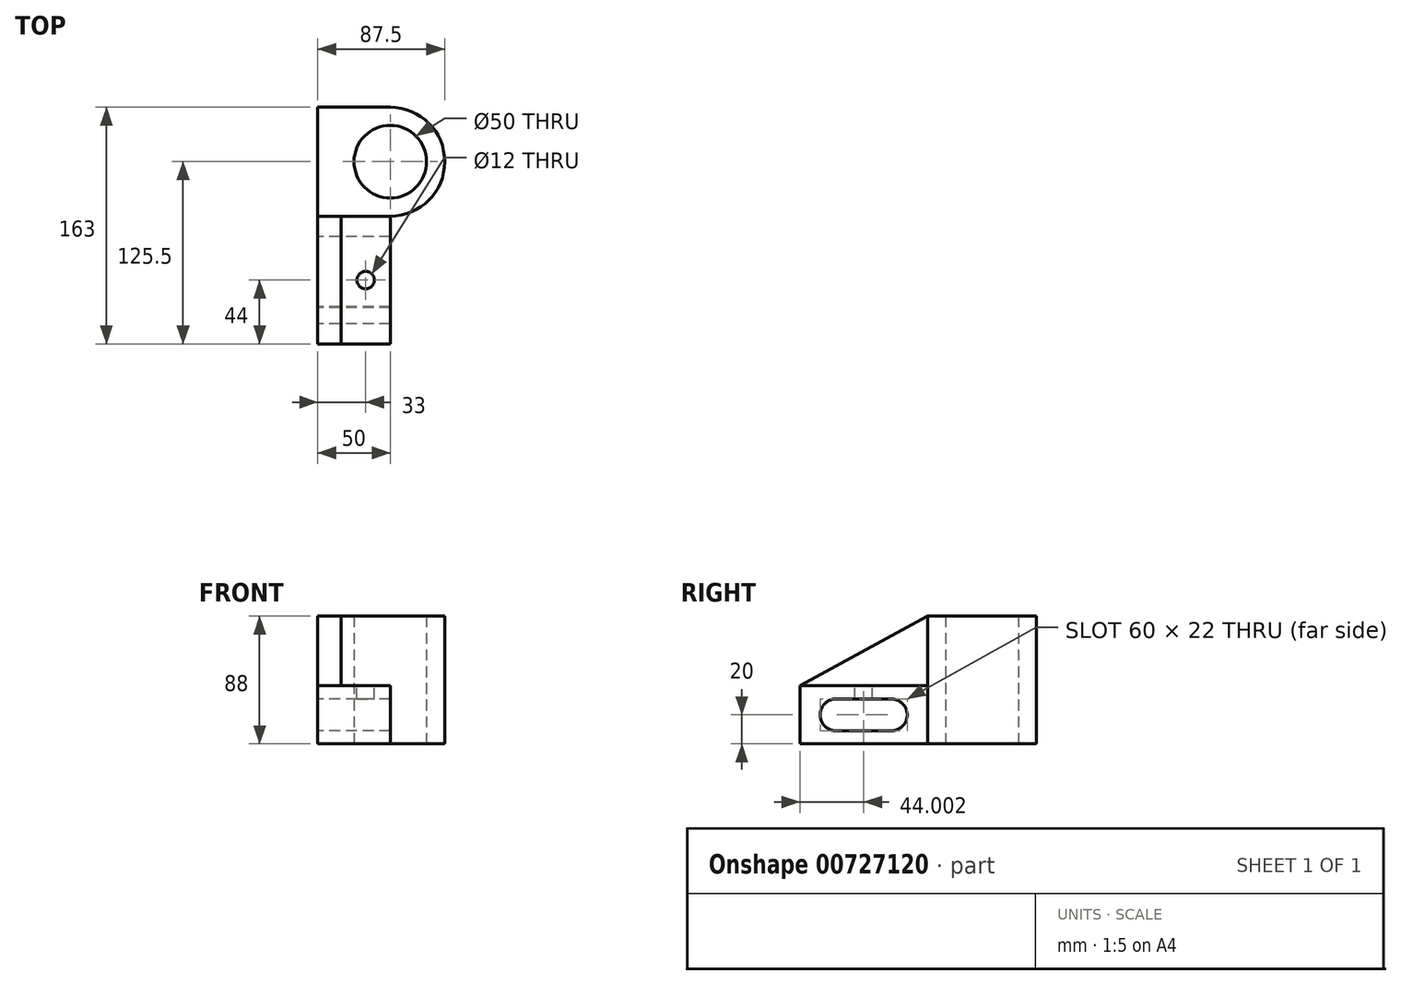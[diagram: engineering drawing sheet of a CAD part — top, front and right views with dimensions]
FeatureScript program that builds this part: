
annotation { "Feature Type Name" : "Feature", "Feature Type Description" : "" }
export const myFeature = defineFeature(function(context is Context, id is Id, definition is map)
    precondition{}
    {
        {
            var Q0;
            Q0=qCreatedBy(makeId("Top.planeOp"),FACE);
            var sketch = newSketch(context, id + "F0", { "sketchPlane" : qUnion([Q0])});
            skLineSegment(sketch, "E0.bottom", {"start": v(0, 0) * mm, "end": v(50, 0) * mm});
            skLineSegment(sketch, "E0.top", {"start": v(0, 75) * mm, "end": v(50, 75) * mm});
            skLineSegment(sketch, "E0.left", {"start": v(0, 0) * mm, "end": v(0, 75) * mm});
            skCircle(sketch, "E1", {"center": v(50, 37.5) * mm, "radius": 25 * mm});
            skCircle(sketch, "E2", {"center": v(50, 37.5) * mm, "radius": 37.5 * mm});
            skSolve(sketch);
        }
        {
            var Q0;
            Q0 = qSketchRegion(id + "F0", true);
            extrude(context, id + "F1", {"entities" : qUnion([Q0]), "depth" : 88 * mm, "offsetDistance" : 25 * mm});
        }
        {
            var Q0;
            Q0=qCreatedBy(makeId("Right.planeOp"),FACE);
            var sketch = newSketch(context, id + "F2", { "sketchPlane" : qUnion([Q0])});
            skLineSegment(sketch, "E3.bottom", {"start": v(0, 0) * mm, "end": v(-88, 0) * mm});
            skLineSegment(sketch, "E3.top", {"start": v(0, 40) * mm, "end": v(-88, 40) * mm});
            skLineSegment(sketch, "E3.left", {"start": v(0, 0) * mm, "end": v(0, 40) * mm});
            skLineSegment(sketch, "E3.right", {"start": v(-88, 0) * mm, "end": v(-88, 40) * mm});
            skLineSegment(sketch, "E4", {"start": v(0, 0) * mm, "end": v(0, 20) * mm});
            skLineSegment(sketch, "E5", {"start": v(0, 20) * mm, "end": v(-25, 20) * mm});
            skArc(sketch, "E6", {"start": v(-25, 9) * mm, "mid": v(-14, 20) * mm, "end": v(-25, 31) * mm});
            skArc(sketch, "E7", {"start": v(-62.86, 31) * mm, "mid": v(-74, 19.72) * mm, "end": v(-62.3, 9.02) * mm});
            skLineSegment(sketch, "E8", {"start": v(-63.72, 9.02) * mm, "end": v(-25, 9) * mm});
            skLineSegment(sketch, "E9", {"start": v(-63.14, 31) * mm, "end": v(-25, 31) * mm});
            skSolve(sketch);
        }
        {
            var Q0;
            Q0 = qSketchRegion(id + "F2", true);
            extrude(context, id + "F3", {"entities" : qUnion([Q0]), "operationType" : NewBodyOperationType.ADD, "depth" : 50 * mm, "offsetDistance" : 25 * mm});
        }
        {
            var Q0;
            Q0=qCreatedBy(makeId("Right.planeOp"),FACE);
            var sketch = newSketch(context, id + "F4", { "sketchPlane" : qUnion([Q0])});
            skLineSegment(sketch, "E10", {"start": v(0, 40) * mm, "end": v(0, 88) * mm});
            skLineSegment(sketch, "E11", {"start": v(0, 40) * mm, "end": v(-88, 40) * mm});
            skLineSegment(sketch, "E12", {"start": v(-88, 40) * mm, "end": v(0, 88) * mm});
            skSolve(sketch);
        }
        {
            var Q0;
            Q0=makeQuery(id+"F4.imprint","IMPRINT",FACE,{"disambiguationData":[TD([[makeQuery(id+"F4.imprint","IMPRINT",EDGE,{"derivedFrom":sQuery(id+"F4.wireOp",EDGE,"E10")}),1.0]])]});
            extrude(context, id + "F5", {"entities" : qUnion([Q0]), "operationType" : NewBodyOperationType.ADD, "depth" : 16 * mm, "offsetDistance" : 25 * mm});
        }
        {
            var Q0;
            Q0=makeQuery(id+"F3.opExtrude","SWEPT_FACE",FACE,{"disambiguationData":[OSD([sQuery(id+"F2.wireOp",EDGE,"E3.top")])]});
            var sketch = newSketch(context, id + "F6", { "sketchPlane" : qUnion([Q0])});
            skCircle(sketch, "E13", {"center": v(33, -44) * mm, "radius": 6 * mm});
            skSolve(sketch);
        }
        {
            var Q0;
            Q0 = qSketchRegion(id + "F6", true);
            extrude(context, id + "F7", {"entities" : qUnion([Q0]), "operationType" : NewBodyOperationType.REMOVE, "endBound" : BoundingType.UP_TO_NEXT, "oppositeDirection" : true, "depth" : 25 * mm, "offsetDistance" : 25 * mm});
        }
    });
